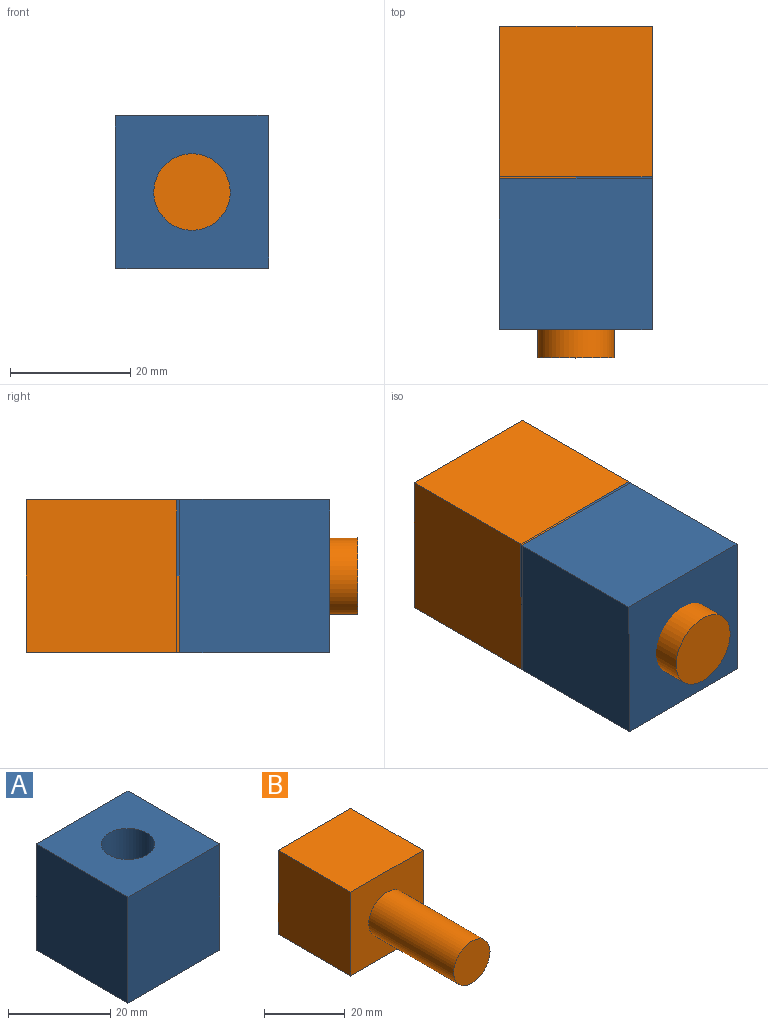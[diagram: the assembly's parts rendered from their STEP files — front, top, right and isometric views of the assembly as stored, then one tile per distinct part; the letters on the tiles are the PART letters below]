
ASSEMBLY  parts=2 mates=1
PART A: 7 faces, bbox 25.4x25.4x25.4 mm
  f0: plane 25.4x25.4mm, normal (1,0,0), area 645.2mm2, adj f1,f3,f4,f5
  f1: plane 25.4x25.4mm, normal (0,1,0), area 645.2mm2, adj f0,f2,f4,f5
  f2: plane 25.4x25.4mm, normal (-1,0,0), area 645.2mm2, adj f1,f3,f4,f5
  f3: plane 25.4x25.4mm, normal (0,-1,0), area 645.2mm2, adj f0,f2,f4,f5
  f4: plane 25.4x25.4mm, normal (0,0,1), area 558.2mm2, adj f0,f1,f2,f3,f6
  f5: plane 25.4x25.4mm, normal (0,0,-1), area 558.2mm2, adj f0,f1,f2,f3,f6
  f6: cylinder r=5.26mm len=25.4mm, axis (0,0,1), area 839.5mm2, adj f4,f5
PART B: 8 faces, bbox 25.4x55.1x25.4 mm
  f0: plane 25.4x25.4mm, normal (0,0,1), area 645.2mm2, adj f1,f3,f4,f5
  f1: plane 25.4x25.4mm, normal (0,-1,0), area 518.5mm2, adj f0,f2,f4,f5,f6
  f2: plane 25.4x25.4mm, normal (0,0,-1), area 645.2mm2, adj f1,f3,f4,f5
  f3: plane 25.4x25.4mm, normal (0,1,0), area 645.2mm2, adj f0,f2,f4,f5
  f4: plane 25.4x25.4mm, normal (1,0,0), area 645.2mm2, adj f0,f1,f2,f3
  f5: plane 25.4x25.4mm, normal (-1,0,0), area 645.2mm2, adj f0,f1,f2,f3
  f6: cylinder r=6.35mm len=29.72mm, axis (0,1,0), area 1185.7mm2, adj f1,f7
  f7: plane 12.7x12.7mm, normal (0,-1,0), area 126.7mm2, adj f6
PLACE A rot(axis=(1,0,0),90deg) t=(17.73,10.2,-3.83)mm
PLACE B t=(5.03,22.54,-3.83)mm fixed
MATE cylindrical B.f6 <-> A.f6  axis (0,-1,0) through (17.73,-19.88,-3.83)mm
